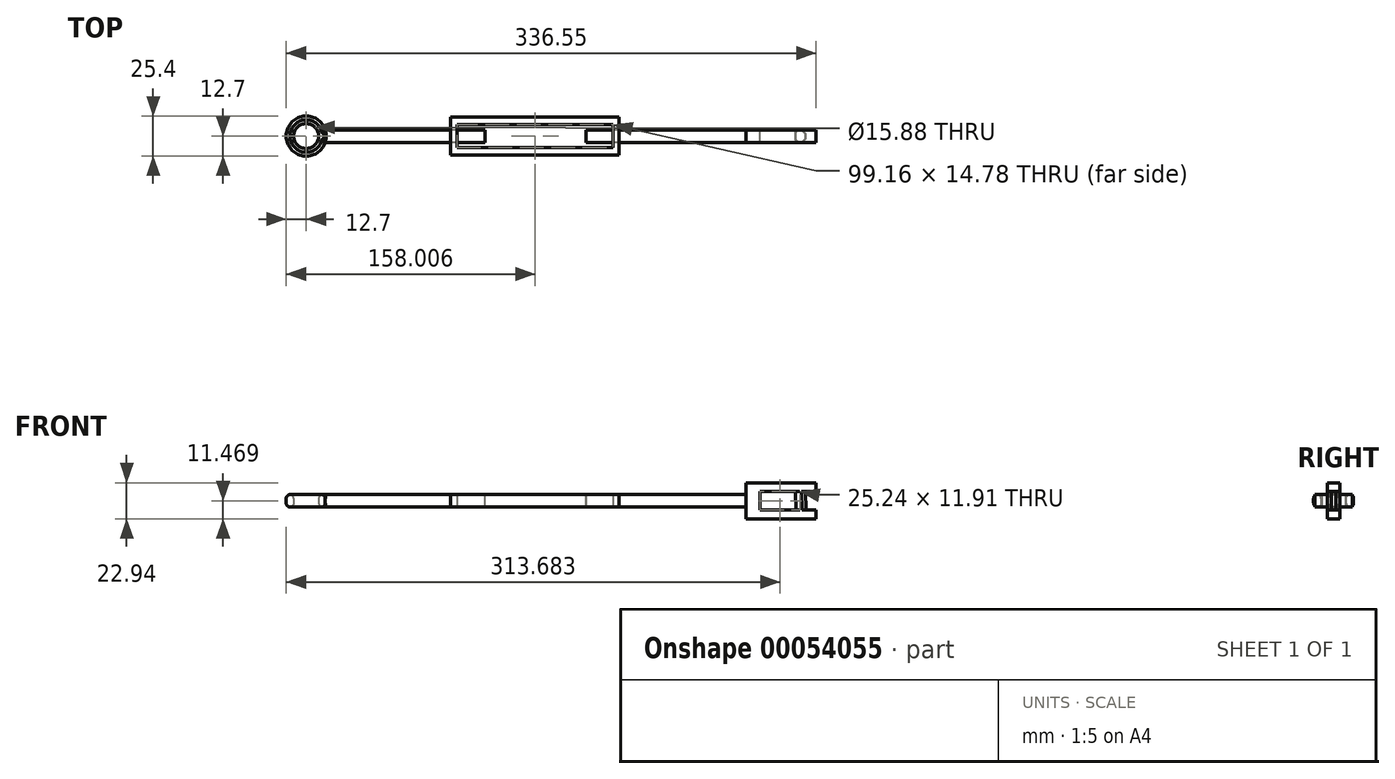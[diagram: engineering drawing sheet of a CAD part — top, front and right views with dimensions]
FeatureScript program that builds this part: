
annotation { "Feature Type Name" : "Feature", "Feature Type Description" : "" }
export const myFeature = defineFeature(function(context is Context, id is Id, definition is map)
    precondition{}
    {
        {
            var Q0;
            Q0=qCreatedBy(makeId("Top.planeOp"),FACE);
            var sketch = newSketch(context, id + "F0", { "sketchPlane" : qUnion([Q0])});
            skCircle(sketch, "E0", {"center": v(0, 0) * mm, "radius": 7.94 * mm});
            skArc(sketch, "E1", {"start": v(12.06, 3.97) * mm, "mid": v(-12.7, 0) * mm, "end": v(12.06, -3.97) * mm});
            skLineSegment(sketch, "E2.rect.bottom", {"start": v(113.66, 3.97) * mm, "end": v(12.06, 3.97) * mm});
            skLineSegment(sketch, "E2.rect.top", {"start": v(113.66, -3.97) * mm, "end": v(12.06, -3.97) * mm});
            skLineSegment(sketch, "E2.rect.left", {"start": v(113.66, 3.97) * mm, "end": v(113.66, -3.97) * mm});
            skPoint(sketch, "E2.rect.middle", {"position": v(62.86, 0) * mm});
            skLineSegment(sketch, "E3.rect.bottom", {"start": v(279.4, 3.97) * mm, "end": v(177.8, 3.97) * mm});
            skLineSegment(sketch, "E3.rect.top", {"start": v(279.4, -3.97) * mm, "end": v(177.8, -3.97) * mm});
            skLineSegment(sketch, "E3.rect.right", {"start": v(177.8, 3.97) * mm, "end": v(177.8, -3.97) * mm});
            skPoint(sketch, "E3.rect.middle", {"position": v(228.6, 0) * mm});
            skLineSegment(sketch, "E4", {"start": v(279.4, 3.97) * mm, "end": v(279.4, -3.97) * mm});
            skSolve(sketch);
        }
        {
            var Q0;
            Q0=makeQuery(id+"F0.imprint","IMPRINT",FACE,{"disambiguationData":[TD([[makeQuery(id+"F0.imprint","IMPRINT",EDGE,{"derivedFrom":sQuery(id+"F0.wireOp",EDGE,"E0")}),-1.0]])]});
            var Q1;
            Q1=makeQuery(id+"F0.imprint","IMPRINT",FACE,{"disambiguationData":[TD([[makeQuery(id+"F0.imprint","IMPRINT",EDGE,{"derivedFrom":sQuery(id+"F0.wireOp",EDGE,"E3.rect.bottom")}),1.0]])]});
            extrude(context, id + "F1", {"entities" : qUnion([Q0, Q1]), "depth" : 7.94 * mm});
        }
        {
            var Q0;
            Q0=qCreatedBy(makeId("Top.planeOp"),FACE);
            var sketch = newSketch(context, id + "F2", { "sketchPlane" : qUnion([Q0])});
            skLineSegment(sketch, "E5.rect.bottom", {"start": v(91.77, -11.95) * mm, "end": v(198.84, -11.95) * mm});
            skLineSegment(sketch, "E5.rect.top", {"start": v(91.77, 11.95) * mm, "end": v(198.84, 11.95) * mm});
            skLineSegment(sketch, "E5.rect.left", {"start": v(91.77, -11.95) * mm, "end": v(91.77, 11.95) * mm});
            skLineSegment(sketch, "E5.rect.right", {"start": v(198.84, -11.95) * mm, "end": v(198.84, 11.95) * mm});
            skPoint(sketch, "E5.rect.middle", {"position": v(145.3, 0) * mm});
            skLineSegment(sketch, "E6.rect.bottom", {"start": v(194.89, 7.39) * mm, "end": v(95.73, 7.39) * mm});
            skLineSegment(sketch, "E6.rect.top", {"start": v(194.89, -7.39) * mm, "end": v(95.73, -7.39) * mm});
            skLineSegment(sketch, "E6.rect.left", {"start": v(194.89, 7.39) * mm, "end": v(194.89, -7.39) * mm});
            skLineSegment(sketch, "E6.rect.right", {"start": v(95.73, 7.39) * mm, "end": v(95.73, -7.39) * mm});
            skSolve(sketch);
        }
        {
            var Q0;
            Q0=makeQuery(id+"F2.imprint","IMPRINT",FACE,{"disambiguationData":[TD([[makeQuery(id+"F2.imprint","IMPRINT",EDGE,{"derivedFrom":sQuery(id+"F2.wireOp",EDGE,"E5.rect.bottom")}),1.0]])]});
            extrude(context, id + "F3", {"entities" : qUnion([Q0]), "depth" : 7.94 * mm});
        }
        {
            var Q0;
            Q0=makeQuery(id+"F1.opExtrude","CAP_EDGE",EDGE,{"disambiguationData":[OSD([sQuery(id+"F0.wireOp",EDGE,"E2.rect.top")])],"isStart":false});
            var Q1;
            Q1=makeQuery(id+"F1.opExtrude","CAP_EDGE",EDGE,{"disambiguationData":[OSD([sQuery(id+"F0.wireOp",EDGE,"E2.rect.bottom")])],"isStart":false});
            var Q2;
            Q2=makeQuery(id+"F1.opExtrude","CAP_EDGE",EDGE,{"disambiguationData":[OSD([sQuery(id+"F0.wireOp",EDGE,"E3.rect.bottom")])],"isStart":false});
            var Q3;
            Q3=makeQuery(id+"F1.opExtrude","CAP_EDGE",EDGE,{"disambiguationData":[OSD([sQuery(id+"F0.wireOp",EDGE,"E3.rect.top")])],"isStart":false});
            var Q4;
            Q4=makeQuery(id+"F1.opExtrude","CAP_EDGE",EDGE,{"disambiguationData":[OSD([sQuery(id+"F0.wireOp",EDGE,"E2.rect.top")])],"isStart":true});
            var Q5;
            Q5=makeQuery(id+"F1.opExtrude","CAP_EDGE",EDGE,{"disambiguationData":[OSD([sQuery(id+"F0.wireOp",EDGE,"E2.rect.bottom")])],"isStart":true});
            var Q6;
            Q6=makeQuery(id+"F1.opExtrude","CAP_EDGE",EDGE,{"disambiguationData":[OSD([sQuery(id+"F0.wireOp",EDGE,"E3.rect.top")])],"isStart":true});
            var Q7;
            Q7=makeQuery(id+"F1.opExtrude","CAP_EDGE",EDGE,{"disambiguationData":[OSD([sQuery(id+"F0.wireOp",EDGE,"E3.rect.bottom")])],"isStart":true});
            fillet(context, id + "F4", {"entities" : qUnion([Q0, Q1, Q2, Q3, Q4, Q5, Q6, Q7]), "radius" : 3.97 * mm, "tangentPropagation" : true, "allowEdgeOverflow" : false});
        }
        {
            var Q0;
            Q0=qCreatedBy(makeId("Front.planeOp"),FACE);
            var sketch = newSketch(context, id + "F5", { "sketchPlane" : qUnion([Q0])});
            skLineSegment(sketch, "E7.rect.bottom", {"start": v(323.85, 15.44) * mm, "end": v(279.4, 15.44) * mm});
            skLineSegment(sketch, "E7.rect.top", {"start": v(323.85, -7.5) * mm, "end": v(279.4, -7.5) * mm});
            skLineSegment(sketch, "E7.rect.left", {"start": v(323.85, 15.44) * mm, "end": v(323.85, 9.92) * mm});
            skLineSegment(sketch, "E7.rect.right", {"start": v(279.4, 15.44) * mm, "end": v(279.4, -7.5) * mm});
            skPoint(sketch, "E7.rect.middle", {"position": v(301.63, 3.97) * mm});
            skLineSegment(sketch, "E8", {"start": v(160.13, 3.97) * mm, "end": v(301.63, 3.97) * mm, "construction": true});
            skLineSegment(sketch, "E9.rect.bottom", {"start": v(323.85, 9.92) * mm, "end": v(317.06, 9.92) * mm});
            skLineSegment(sketch, "E9.rect.top", {"start": v(323.85, -1.98) * mm, "end": v(317.42, -1.98) * mm});
            skLineSegment(sketch, "E9.rect.right", {"start": v(288.36, 9.92) * mm, "end": v(288.36, -1.98) * mm});
            skPoint(sketch, "E9.rect.middle", {"position": v(306.1, 3.97) * mm});
            skLineSegment(sketch, "E10.trimOffspring", {"start": v(323.85, -1.98) * mm, "end": v(323.85, -7.5) * mm});
            skLineSegment(sketch, "E11.left", {"start": v(310.71, 9.92) * mm, "end": v(311.06, -1.98) * mm});
            skLineSegment(sketch, "E11.right", {"start": v(317.06, 9.92) * mm, "end": v(317.42, -1.98) * mm});
            skLineSegment(sketch, "E12.trimOffspring", {"start": v(310.71, 9.92) * mm, "end": v(288.36, 9.92) * mm});
            skLineSegment(sketch, "E13.trimOffspring", {"start": v(311.06, -1.98) * mm, "end": v(288.36, -1.98) * mm});
            skPoint(sketch, "E14", {"position": v(310.89, 3.97) * mm});
            skSolve(sketch);
        }
        {
            var Q0;
            Q0=makeQuery(id+"F5.imprint","IMPRINT",FACE,{"disambiguationData":[TD([[makeQuery(id+"F5.imprint","IMPRINT",EDGE,{"derivedFrom":sQuery(id+"F5.wireOp",EDGE,"E7.rect.bottom")}),1.0]])]});
            extrude(context, id + "F6", {"entities" : qUnion([Q0]), "operationType" : NewBodyOperationType.ADD, "depth" : 7.94 * mm, "symmetric" : true});
        }
        {
            var Q0;
            Q0=makeQuery(id+"F1.opExtrude","CAP_EDGE",EDGE,{"disambiguationData":[OSD([sQuery(id+"F0.wireOp",EDGE,"E1")])],"isStart":true});
            var Q1;
            Q1=makeQuery(id+"F1.opExtrude","CAP_EDGE",EDGE,{"disambiguationData":[OSD([sQuery(id+"F0.wireOp",EDGE,"E0")])],"isStart":true});
            var Q2;
            Q2=makeQuery(id+"F1.opExtrude","CAP_FACE",FACE,{"disambiguationData":[OSD([sQuery(id+"F0.wireOp",EDGE,"E0"),sQuery(id+"F0.wireOp",EDGE,"E1"),sQuery(id+"F0.wireOp",EDGE,"E2.rect.bottom"),sQuery(id+"F0.wireOp",EDGE,"E2.rect.top"),sQuery(id+"F0.wireOp",EDGE,"E2.rect.left")])],"isStart":false});
            var Q3;
            Q3=makeQuery(id+"F1.opExtrude","CAP_EDGE",EDGE,{"disambiguationData":[OSD([sQuery(id+"F0.wireOp",EDGE,"E0")])],"isStart":false});
            var Q4;
            Q4=makeQuery(id+"F1.opExtrude","CAP_EDGE",EDGE,{"disambiguationData":[OSD([sQuery(id+"F0.wireOp",EDGE,"16564bac-1533-40ef-aac4-bf0d4e937146.right")])],"isStart":false});
            var Q5;
            Q5=makeQuery(id+"F1.opExtrude","CAP_EDGE",EDGE,{"disambiguationData":[OSD([sQuery(id+"F0.wireOp",EDGE,"16564bac-1533-40ef-aac4-bf0d4e937146.left")])],"isStart":false});
            var Q6;
            Q6=makeQuery(id+"F1.opExtrude","CAP_EDGE",EDGE,{"disambiguationData":[OSD([sQuery(id+"F0.wireOp",EDGE,"16564bac-1533-40ef-aac4-bf0d4e937146.left")])],"isStart":true});
            var Q7;
            Q7=makeQuery(id+"F1.opExtrude","CAP_EDGE",EDGE,{"disambiguationData":[OSD([sQuery(id+"F0.wireOp",EDGE,"16564bac-1533-40ef-aac4-bf0d4e937146.right")])],"isStart":true});
            var Q8;
            Q8=makeQuery(id+"F6.opExtrude","CAP_EDGE",EDGE,{"disambiguationData":[OSD([sQuery(id+"F5.wireOp",EDGE,"E11.left")])],"isStart":false});
            var Q9;
            Q9=makeQuery(id+"F6.opExtrude","CAP_EDGE",EDGE,{"disambiguationData":[OSD([sQuery(id+"F5.wireOp",EDGE,"E11.left")])],"isStart":true});
            fillet(context, id + "F7", {"entities" : qUnion([Q0, Q1, Q2, Q3, Q4, Q5, Q6, Q7, Q8, Q9]), "radius" : 2.54 * mm, "tangentPropagation" : true, "allowEdgeOverflow" : false});
        }
        {
            var Q0;
            Q0=makeQuery(id+"F6.opExtrude","CAP_EDGE",EDGE,{"disambiguationData":[OSD([sQuery(id+"F5.wireOp",EDGE,"E11.right")])],"isStart":false});
            var Q1;
            Q1=makeQuery(id+"F6.opExtrude","CAP_EDGE",EDGE,{"disambiguationData":[OSD([sQuery(id+"F5.wireOp",EDGE,"E11.right")])],"isStart":true});
            chamfer(context, id + "F8", {"entities" : qUnion([Q0, Q1]), "width" : 2.54 * mm, "tangentPropagation" : true});
        }
    });
